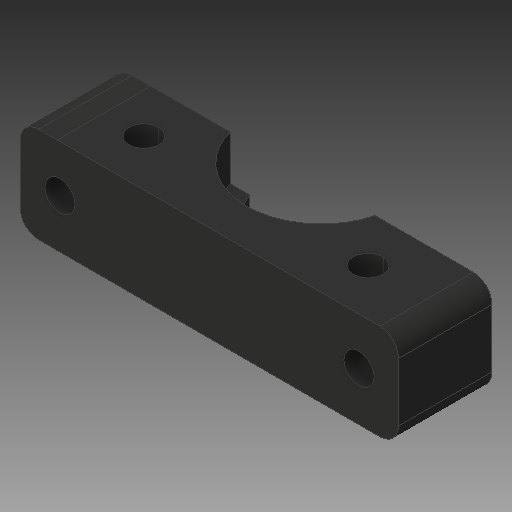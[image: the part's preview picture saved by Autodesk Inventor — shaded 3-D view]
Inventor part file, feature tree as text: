
AUTODESK INVENTOR PART (.ipt)
format: ipt  version: 2017 (Build 210142000, 142)  size: 185,344 bytes
history: native  units: mm
features: sketch x9, other x3
ambient origin geometry x8: Origin, YZ Plane, XZ Plane, XY Plane, X Axis, Y Axis, Z Axis, Center Point
bodies: Solid1 (feature_tree)
feature tree (12):
  other  "Hotend Clamp P2.ipt"
  other  "Solid1::Hotend Clamp P2.ipt"
  other  "TaggingFeature1"
  sketch  "Sketch1"  dims[d0=10.0mm]
  sketch  "Sketch2"
  sketch  "Sketch3"
  sketch  "Sketch4"
  sketch  "Sketch5"
  sketch  "Sketch6"
  sketch  "Sketch7"
  sketch  "Sketch8"
  sketch  "Sketch9"
